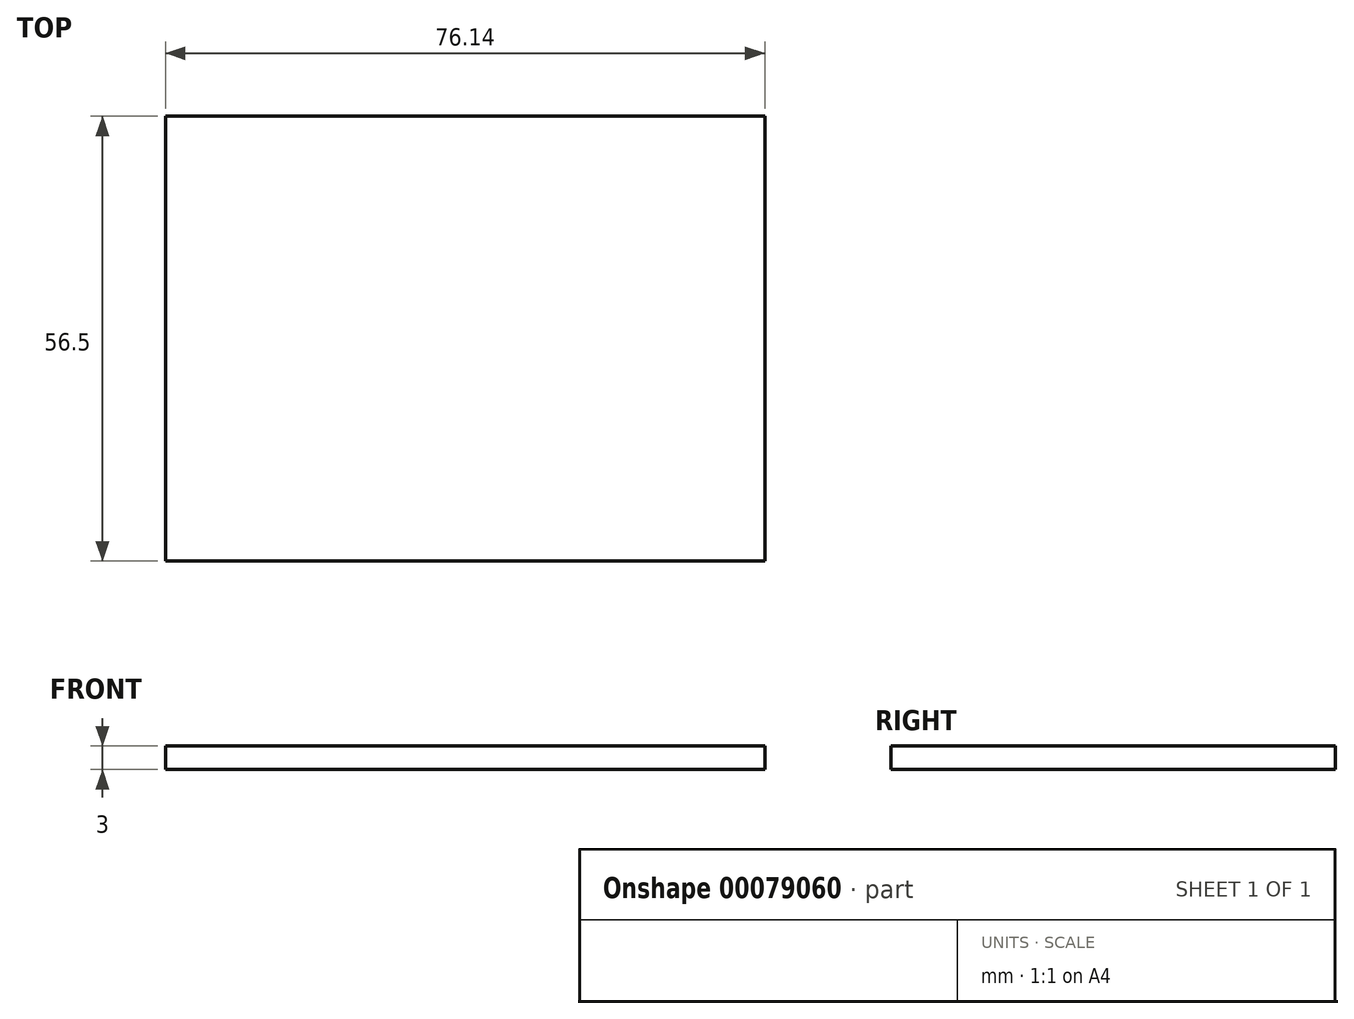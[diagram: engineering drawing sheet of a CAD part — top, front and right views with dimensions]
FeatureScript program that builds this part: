
annotation { "Feature Type Name" : "Feature", "Feature Type Description" : "" }
export const myFeature = defineFeature(function(context is Context, id is Id, definition is map)
    precondition{}
    {
        {
            var Q0;
            Q0=qCreatedBy(makeId("Top.planeOp"),FACE);
            var sketch = newSketch(context, id + "F0", { "sketchPlane" : qUnion([Q0])});
            skLineSegment(sketch, "E0.bottom", {"start": v(-76.14, 56.5) * mm, "end": v(0, 56.5) * mm});
            skLineSegment(sketch, "E0.top", {"start": v(-76.14, 0) * mm, "end": v(0, 0) * mm});
            skLineSegment(sketch, "E0.left", {"start": v(-76.14, 56.5) * mm, "end": v(-76.14, 0) * mm});
            skLineSegment(sketch, "E0.right", {"start": v(0, 56.5) * mm, "end": v(0, 0) * mm});
            skSolve(sketch);
        }
        {
            var Q0;
            Q0 = qSketchRegion(id + "F0", true);
            extrude(context, id + "F1", {"entities" : qUnion([Q0]), "depth" : 3 * mm});
        }
    });
